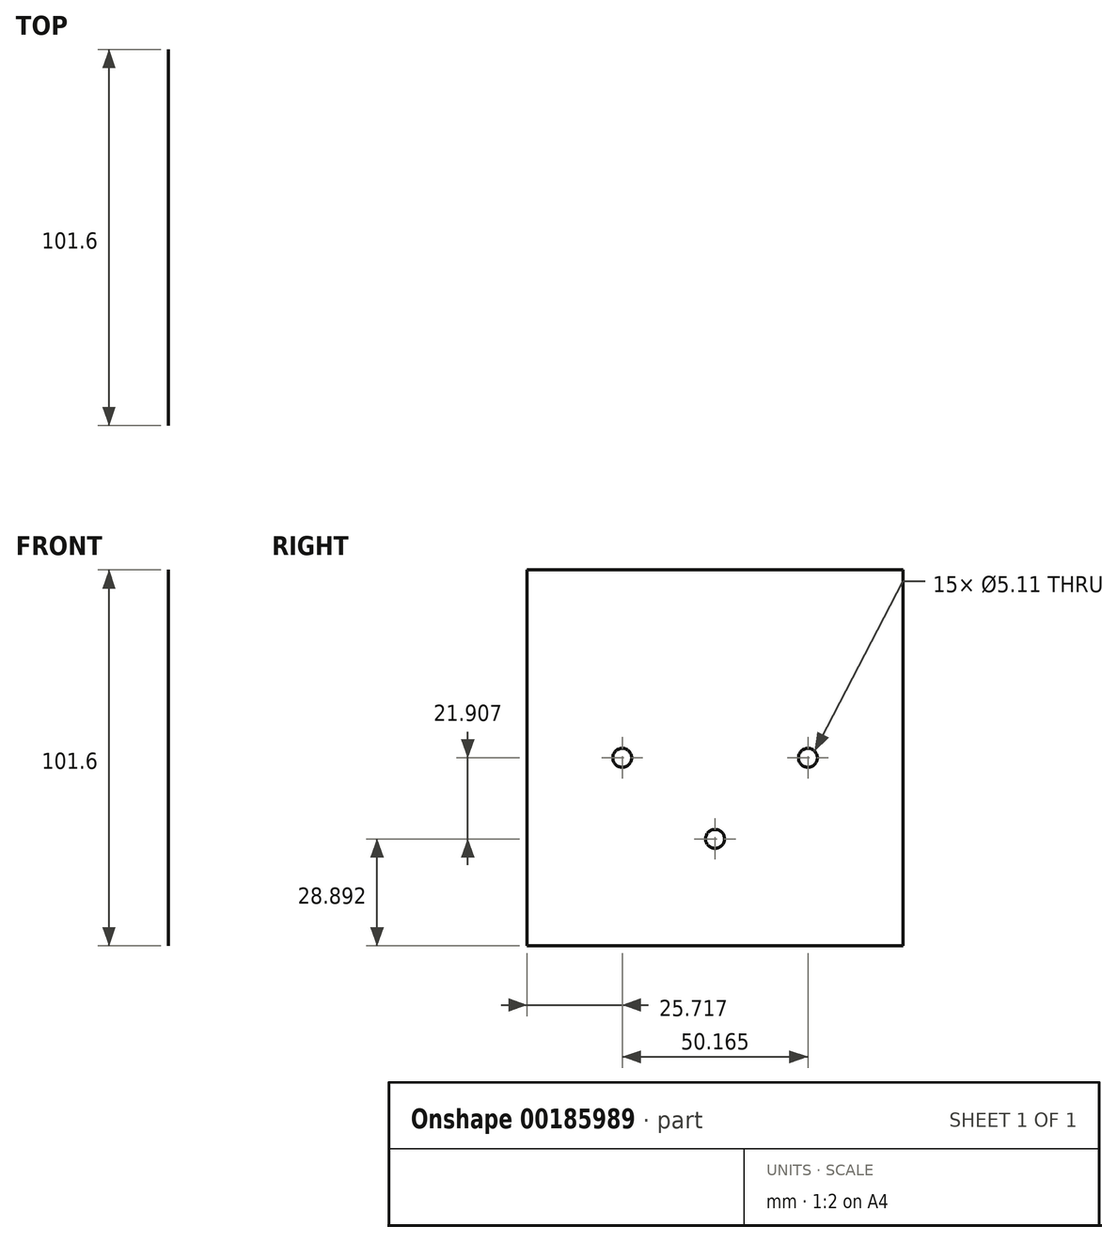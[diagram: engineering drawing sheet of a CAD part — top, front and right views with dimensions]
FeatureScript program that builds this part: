
annotation { "Feature Type Name" : "Feature", "Feature Type Description" : "" }
export const myFeature = defineFeature(function(context is Context, id is Id, definition is map)
    precondition{}
    {
        {
            var Q0;
            Q0=qCreatedBy(makeId("Right.planeOp"),FACE);
            var sketch = newSketch(context, id + "F0", { "sketchPlane" : qUnion([Q0])});
            skLineSegment(sketch, "E0.bottom", {"start": v(50.8, -50.8) * mm, "end": v(-50.8, -50.8) * mm});
            skLineSegment(sketch, "E0.top", {"start": v(50.8, 50.8) * mm, "end": v(-50.8, 50.8) * mm});
            skLineSegment(sketch, "E0.left", {"start": v(50.8, -50.8) * mm, "end": v(50.8, 50.8) * mm});
            skLineSegment(sketch, "E0.right", {"start": v(-50.8, -50.8) * mm, "end": v(-50.8, 50.8) * mm});
            skPoint(sketch, "E0.middle", {"position": v(0, 0) * mm});
            skSolve(sketch);
        }
        {
            var Q0;
            Q0 = qSketchRegion(id + "F0", true);
            extrude(context, id + "F1", {"entities" : qUnion([Q0]), "depth" : 1 / 203.2 * mm});
        }
        {
            var Q0;
            Q0=makeQuery(id+"F1.opExtrude","CAP_FACE",FACE,{"disambiguationData":[OSD([sQuery(id+"F0.wireOp",EDGE,"E0.bottom"),sQuery(id+"F0.wireOp",EDGE,"E0.top"),sQuery(id+"F0.wireOp",EDGE,"E0.left"),sQuery(id+"F0.wireOp",EDGE,"E0.right")])],"isStart":false});
            var sketch = newSketch(context, id + "F2", { "sketchPlane" : qUnion([Q0])});
            skPoint(sketch, "E1", {"position": v(0, -21.9) * mm});
            skPoint(sketch, "E2", {"position": v(-25.08, 0) * mm});
            skPoint(sketch, "E2.positionSnap0", {"position": v(50.8, 0) * mm});
            skPoint(sketch, "E3", {"position": v(25.08, 0) * mm});
            skSolve(sketch);
        }
        {
            var Q0;
            Q0=sQuery(id+"F2.wireOp",VERTEX,"E1");
            var Q1;
            Q1=sQuery(id+"F2.wireOp",VERTEX,"E2");
            var Q2;
            Q2=sQuery(id+"F2.wireOp",VERTEX,"E3");
            var Q3;
            Q3=makeQuery(id+"F1.opExtrude","SWEPT_BODY",BODY,{"disambiguationData":[OSD([sQuery(id+"F0.wireOp",EDGE,"E0.bottom"),sQuery(id+"F0.wireOp",EDGE,"E0.top"),sQuery(id+"F0.wireOp",EDGE,"E0.left"),sQuery(id+"F0.wireOp",EDGE,"E0.right")])]});
            hole(context, id + "F3", {"style" : HoleStyle.SIMPLE, "endStyle" : HoleEndStyle.BLIND, "standardTappedOrClearance" : lookupTablePath({ "standard" : "ANSI", "fit" : "Normal (ASME)", "size" : "#10", "type" : "Clearance" }), "standardBlindInLast" : lookupTablePath({ "fit" : "Free", "standard" : "ANSI", "size" : "#10", "type" : "Clearance" }), "holeDiameter" : 5.1 * mm, "holeDepth" : 25 * mm, "locations" : qUnion([Q0, Q1, Q2]), "scope" : qUnion([Q3])});
        }
    });
